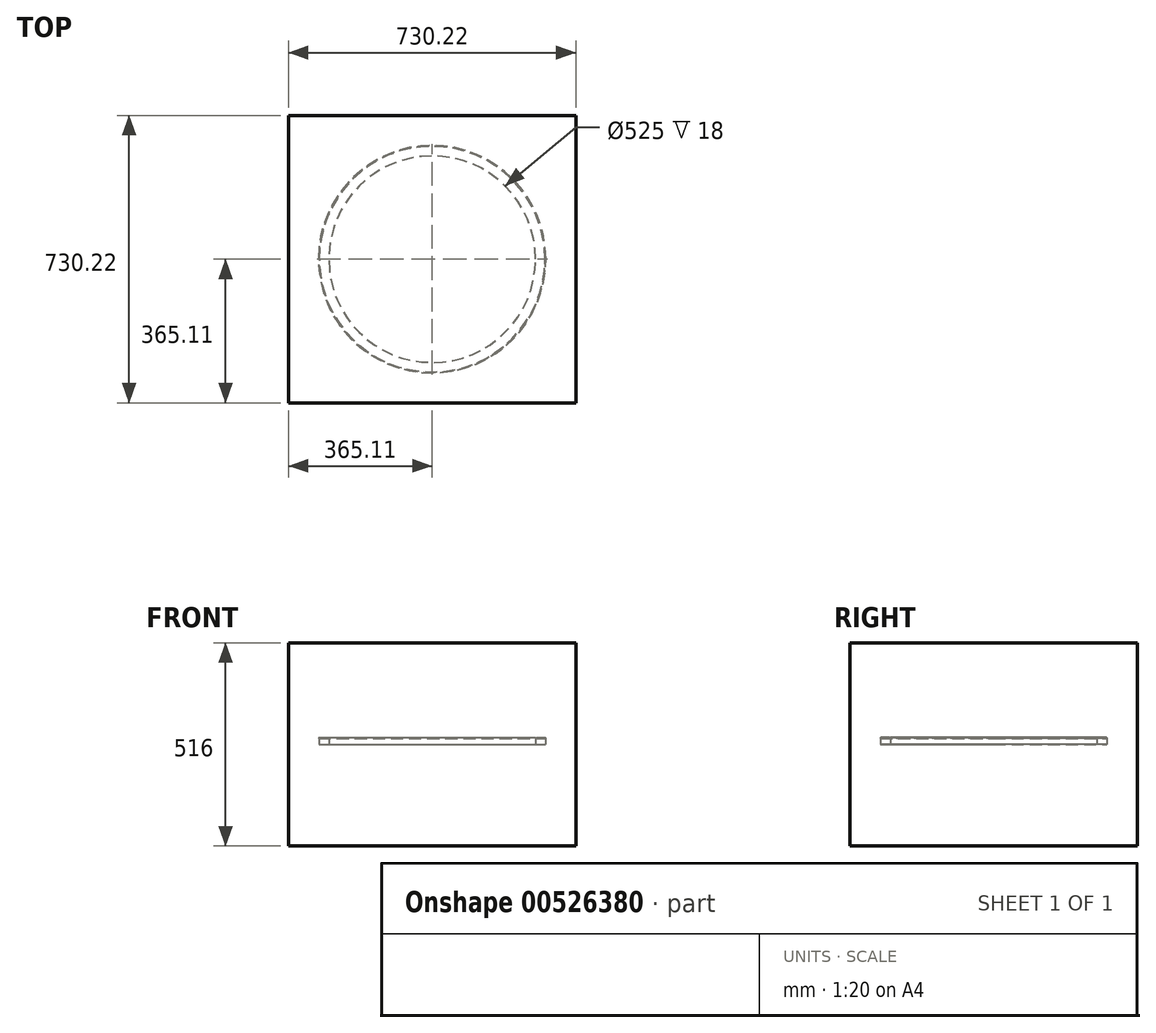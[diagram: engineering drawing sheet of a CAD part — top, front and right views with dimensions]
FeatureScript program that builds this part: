
annotation { "Feature Type Name" : "Feature", "Feature Type Description" : "" }
export const myFeature = defineFeature(function(context is Context, id is Id, definition is map)
    precondition{}
    {
        {
            var Q0;
            Q0=qCreatedBy(makeId("Front.planeOp"),FACE);
            var sketch = newSketch(context, id + "F0", { "sketchPlane" : qUnion([Q0])});
            skLineSegment(sketch, "E0", {"start": v(-262.5, 0) * mm, "end": v(-262.5, 18) * mm});
            skLineSegment(sketch, "E1", {"start": v(-262.5, 18) * mm, "end": v(-286.75, 18) * mm});
            skLineSegment(sketch, "E2", {"start": v(-286.75, 18) * mm, "end": v(-288.75, 16) * mm});
            skLineSegment(sketch, "E3", {"start": v(-288.75, 16) * mm, "end": v(-287.7, 16) * mm});
            skLineSegment(sketch, "E4", {"start": v(-287.7, 16) * mm, "end": v(-287.7, 0) * mm});
            skLineSegment(sketch, "E5", {"start": v(-287.7, 0) * mm, "end": v(-262.5, 0) * mm});
            skLineSegment(sketch, "E6", {"start": v(0, 0) * mm, "end": v(0, 18) * mm, "construction": true});
            skSolve(sketch);
        }
        {
            var Q0;
            Q0 = qSketchRegion(id + "F0", true);
            var Q1;
            Q1=sQuery(id+"F0.wireOp",EDGE,"E6");
            revolve(context, id + "F1", {"entities" : qUnion([Q0]), "axis" : qUnion([Q1]), "revolveType" : RevolveType.FULL});
        }
        {
            var Q0;
            Q0=qCreatedBy(makeId("Top.planeOp"),FACE);
            var sketch = newSketch(context, id + "F2", { "sketchPlane" : qUnion([Q0])});
            skLineSegment(sketch, "E7.bottom", {"start": v(-365.11, -365.11) * mm, "end": v(365.11, -365.11) * mm});
            skLineSegment(sketch, "E7.top", {"start": v(-365.11, 365.11) * mm, "end": v(365.11, 365.11) * mm});
            skLineSegment(sketch, "E7.left", {"start": v(-365.11, -365.11) * mm, "end": v(-365.11, 365.11) * mm});
            skLineSegment(sketch, "E7.right", {"start": v(365.11, -365.11) * mm, "end": v(365.11, 365.11) * mm});
            skPoint(sketch, "E7.middle", {"position": v(0, 0) * mm});
            skSolve(sketch);
        }
        {
            var Q0;
            Q0 = qSketchRegion(id + "F2", true);
            extrude(context, id + "F3", {"entities" : qUnion([Q0]), "endBound" : BoundingType.SYMMETRIC, "depth" : 516 * mm, "offsetDistance" : 25 * mm});
        }
    });
